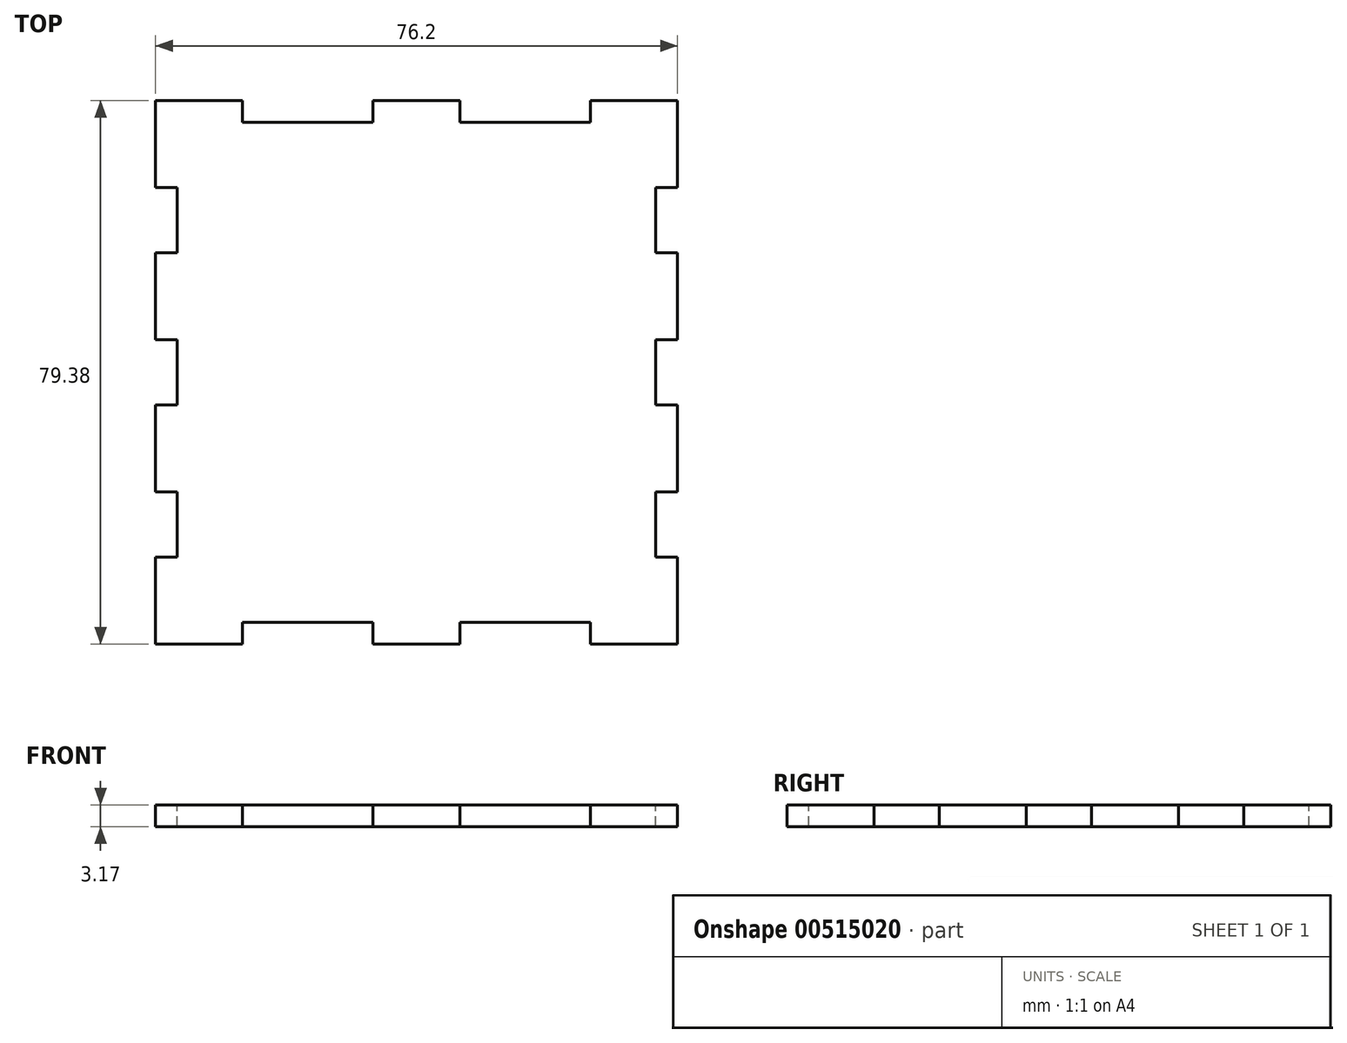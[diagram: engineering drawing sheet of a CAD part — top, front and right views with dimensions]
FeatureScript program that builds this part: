
annotation { "Feature Type Name" : "Feature", "Feature Type Description" : "" }
export const myFeature = defineFeature(function(context is Context, id is Id, definition is map)
    precondition{}
    {
        {
            var Q0;
            Q0=qCreatedBy(makeId("Top.planeOp"),FACE);
            var sketch = newSketch(context, id + "F0", { "sketchPlane" : qUnion([Q0])});
            skLineSegment(sketch, "E0.bottom", {"start": v(-38.1, 39.69) * mm, "end": v(38.1, 39.69) * mm});
            skLineSegment(sketch, "E0.top", {"start": v(-38.1, -39.69) * mm, "end": v(38.1, -39.69) * mm});
            skLineSegment(sketch, "E0.left", {"start": v(-38.1, 39.69) * mm, "end": v(-38.1, -39.69) * mm});
            skLineSegment(sketch, "E0.right", {"start": v(38.1, 39.69) * mm, "end": v(38.1, -39.69) * mm});
            skSolve(sketch);
        }
        {
            var Q0;
            Q0 = qSketchRegion(id + "F0", true);
            extrude(context, id + "F1", {"entities" : qUnion([Q0]), "depth" : 3.17 * mm, "offsetDistance" : 25.4 * mm});
        }
        {
            var Q0;
            Q0=makeQuery(id+"F1.opExtrude","CAP_FACE",FACE,{"disambiguationData":[OSD([sQuery(id+"F0.wireOp",EDGE,"E0.bottom"),sQuery(id+"F0.wireOp",EDGE,"E0.top"),sQuery(id+"F0.wireOp",EDGE,"E0.left"),sQuery(id+"F0.wireOp",EDGE,"E0.right")])],"isStart":false});
            var sketch = newSketch(context, id + "F2", { "sketchPlane" : qUnion([Q0])});
            skLineSegment(sketch, "E1", {"start": v(-38.1, 0) * mm, "end": v(38.1, 0) * mm, "construction": true});
            skLineSegment(sketch, "E2.bottom", {"start": v(-25.4, 39.69) * mm, "end": v(-6.35, 39.69) * mm});
            skLineSegment(sketch, "E2.top", {"start": v(-25.4, 36.51) * mm, "end": v(-6.35, 36.51) * mm});
            skLineSegment(sketch, "E2.left", {"start": v(-25.4, 39.69) * mm, "end": v(-25.4, 36.51) * mm});
            skLineSegment(sketch, "E2.right", {"start": v(-6.35, 39.69) * mm, "end": v(-6.35, 36.51) * mm});
            skLineSegment(sketch, "E3.1.0.0", {"start": v(6.35, 36.51) * mm, "end": v(25.4, 36.51) * mm});
            skLineSegment(sketch, "E3.1.0.1", {"start": v(6.35, 39.69) * mm, "end": v(25.4, 39.69) * mm});
            skLineSegment(sketch, "E3.1.0.2", {"start": v(25.4, 39.69) * mm, "end": v(25.4, 36.51) * mm});
            skLineSegment(sketch, "E3.1.0.3", {"start": v(6.35, 39.69) * mm, "end": v(6.35, 36.51) * mm});
            skLineSegment(sketch, "E3.direction1", {"start": v(-25.4, 36.51) * mm, "end": v(6.35, 36.51) * mm, "construction": true});
            skLineSegment(sketch, "E4.MirrorCS", {"start": v(25.4, -39.69) * mm, "end": v(25.4, -36.51) * mm});
            skLineSegment(sketch, "E5.MirrorCS", {"start": v(6.35, -39.69) * mm, "end": v(6.35, -36.51) * mm});
            skLineSegment(sketch, "E6.MirrorCS", {"start": v(-25.4, -39.69) * mm, "end": v(-25.4, -36.51) * mm});
            skLineSegment(sketch, "E7.MirrorCS", {"start": v(-6.35, -39.69) * mm, "end": v(-6.35, -36.51) * mm});
            skLineSegment(sketch, "E8.MirrorCS", {"start": v(-25.4, -36.51) * mm, "end": v(-6.35, -36.51) * mm});
            skLineSegment(sketch, "E9.MirrorCS", {"start": v(-25.4, -39.69) * mm, "end": v(-6.35, -39.69) * mm});
            skLineSegment(sketch, "E10.MirrorCS", {"start": v(6.35, -39.69) * mm, "end": v(25.4, -39.69) * mm});
            skLineSegment(sketch, "E11.MirrorCS", {"start": v(-25.4, -36.51) * mm, "end": v(6.35, -36.51) * mm, "construction": true});
            skLineSegment(sketch, "E12.MirrorCS", {"start": v(6.35, -36.51) * mm, "end": v(25.4, -36.51) * mm});
            skSolve(sketch);
        }
        {
            var Q0;
            Q0 = qSketchRegion(id + "F2", true);
            extrude(context, id + "F3", {"entities" : qUnion([Q0]), "operationType" : NewBodyOperationType.REMOVE, "endBound" : BoundingType.THROUGH_ALL, "oppositeDirection" : true, "depth" : 25.4 * mm, "offsetDistance" : 25.4 * mm});
        }
        {
            var Q0;
            Q0=makeQuery(id+"F1.opExtrude","CAP_FACE",FACE,{"disambiguationData":[OSD([sQuery(id+"F0.wireOp",EDGE,"E0.bottom"),sQuery(id+"F0.wireOp",EDGE,"E0.top"),sQuery(id+"F0.wireOp",EDGE,"E0.left"),sQuery(id+"F0.wireOp",EDGE,"E0.right")])],"isStart":false});
            var sketch = newSketch(context, id + "F4", { "sketchPlane" : qUnion([Q0])});
            skLineSegment(sketch, "E13.bottom", {"start": v(-38.1, 26.99) * mm, "end": v(-34.93, 26.99) * mm});
            skLineSegment(sketch, "E13.top", {"start": v(-38.1, 17.46) * mm, "end": v(-34.93, 17.46) * mm});
            skLineSegment(sketch, "E13.left", {"start": v(-38.1, 26.99) * mm, "end": v(-38.1, 17.46) * mm});
            skLineSegment(sketch, "E13.right", {"start": v(-34.93, 26.99) * mm, "end": v(-34.93, 17.46) * mm});
            skLineSegment(sketch, "E14.0.1.0", {"start": v(-34.93, 4.76) * mm, "end": v(-34.93, -4.76) * mm});
            skLineSegment(sketch, "E14.0.1.1", {"start": v(-38.1, 4.76) * mm, "end": v(-38.1, -4.76) * mm});
            skLineSegment(sketch, "E14.0.1.2", {"start": v(-38.1, 4.76) * mm, "end": v(-34.93, 4.76) * mm});
            skLineSegment(sketch, "E14.0.1.3", {"start": v(-38.1, -4.76) * mm, "end": v(-34.93, -4.76) * mm});
            skLineSegment(sketch, "E14.0.2.0", {"start": v(-34.93, -17.46) * mm, "end": v(-34.93, -26.99) * mm});
            skLineSegment(sketch, "E14.0.2.1", {"start": v(-38.1, -17.46) * mm, "end": v(-38.1, -26.99) * mm});
            skLineSegment(sketch, "E14.0.2.2", {"start": v(-38.1, -17.46) * mm, "end": v(-34.93, -17.46) * mm});
            skLineSegment(sketch, "E14.0.2.3", {"start": v(-38.1, -26.99) * mm, "end": v(-34.93, -26.99) * mm});
            skLineSegment(sketch, "E14.direction1", {"start": v(-38.1, 17.46) * mm, "end": v(-12.7, 17.46) * mm, "construction": true});
            skLineSegment(sketch, "E14.direction2", {"start": v(-38.1, 17.46) * mm, "end": v(-38.1, -4.76) * mm, "construction": true});
            skLineSegment(sketch, "E15", {"start": v(0, 39.69) * mm, "end": v(0, -39.69) * mm, "construction": true});
            skLineSegment(sketch, "E16.MirrorCS", {"start": v(38.1, -26.99) * mm, "end": v(34.92, -26.99) * mm});
            skLineSegment(sketch, "E17.MirrorCS", {"start": v(38.1, -4.76) * mm, "end": v(34.93, -4.76) * mm});
            skLineSegment(sketch, "E18.MirrorCS", {"start": v(38.1, 4.76) * mm, "end": v(34.93, 4.76) * mm});
            skLineSegment(sketch, "E19.MirrorCS", {"start": v(38.1, -17.46) * mm, "end": v(34.92, -17.46) * mm});
            skLineSegment(sketch, "E20.MirrorCS", {"start": v(38.1, 26.99) * mm, "end": v(34.93, 26.99) * mm});
            skLineSegment(sketch, "E21.MirrorCS", {"start": v(38.1, 17.46) * mm, "end": v(34.93, 17.46) * mm});
            skLineSegment(sketch, "E22.MirrorCS", {"start": v(38.1, 4.76) * mm, "end": v(38.1, -4.76) * mm});
            skLineSegment(sketch, "E23.MirrorCS", {"start": v(38.1, 17.46) * mm, "end": v(38.1, -4.76) * mm, "construction": true});
            skLineSegment(sketch, "E24.MirrorCS", {"start": v(38.1, 17.46) * mm, "end": v(12.7, 17.46) * mm, "construction": true});
            skLineSegment(sketch, "E25.MirrorCS", {"start": v(34.93, 26.99) * mm, "end": v(34.93, 17.46) * mm});
            skLineSegment(sketch, "E26.MirrorCS", {"start": v(34.93, -17.46) * mm, "end": v(34.93, -26.99) * mm});
            skLineSegment(sketch, "E27.MirrorCS", {"start": v(38.1, 26.99) * mm, "end": v(38.1, 17.46) * mm});
            skLineSegment(sketch, "E28.MirrorCS", {"start": v(34.93, 4.76) * mm, "end": v(34.93, -4.76) * mm});
            skLineSegment(sketch, "E29.MirrorCS", {"start": v(38.1, -17.46) * mm, "end": v(38.1, -26.99) * mm});
            skSolve(sketch);
        }
        {
            var Q0;
            Q0 = qSketchRegion(id + "F4", true);
            extrude(context, id + "F5", {"entities" : qUnion([Q0]), "operationType" : NewBodyOperationType.REMOVE, "endBound" : BoundingType.THROUGH_ALL, "oppositeDirection" : true, "depth" : 25.4 * mm, "offsetDistance" : 25.4 * mm});
        }
    });
